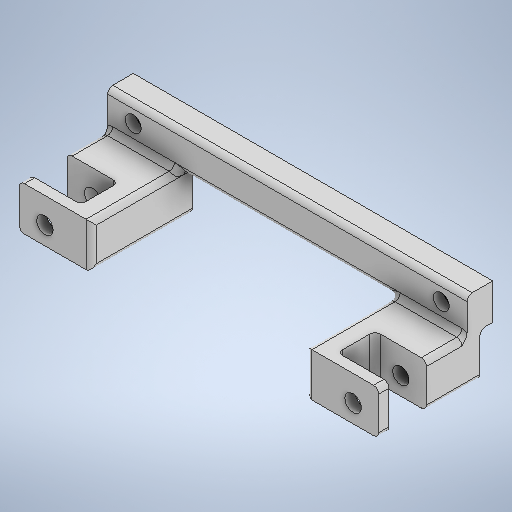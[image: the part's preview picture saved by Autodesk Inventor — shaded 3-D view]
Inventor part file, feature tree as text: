
AUTODESK INVENTOR PART (.ipt)
format: ipt  version: 2025.1 (Build 291241000, 241)  size: 368,128 bytes
history: native  units: mm
features: extrude x5, sketch x3, plane x1, fillet x1, mirror x1, projected_geometry x1
ambient origin geometry x8: Origin, YZ Plane, XZ Plane, XY Plane, X Axis, Y Axis, Z Axis, Center Point
bodies: Solid1 (feature_tree)
feature tree (12):
  sketch  "Sketch1"  dims[d0=4.85mm d1=30.0mm]
  extrude  "Extrusion1"  Depth=30.0mm
  extrude  "Extrusion2"  Depth=3.2mm
  extrude  "Extrusion3"  Depth=1.0mm
  extrude  "Extrusion4"  Depth=1.0mm
  plane  "Work Plane1"
  extrude  "Extrusion5"  TaperAngle=0.0deg  [1 undecoded]
  fillet  "Fillet1"  Radius=3.5mm
  mirror  "Mirror1"
  sketch  "Sketch2"  dims[d2=3.1mm d3=3.2mm]
  sketch  "Sketch4"  dims[d4=0.0mm d5=8.5mm d6=35.0mm d7=0.0mm d8=3.5mm d9=3.5mm d10=0.0mm d11=14.0mm d12=3.5mm d13=4.0mm d14=5.0mm d15=0.0mm d16=3.0mm d17=0.0mm d18=2.5mm d19=0.0mm d20=17.2mm d21=0.0mm d22=-2.0mm d23=5.0mm d24=7.3mm d25=0.0mm d26=1.0mm]
  projected_geometry  "Projected Loop1"
note: 1 required parameter value undecoded (feature->parameter linkage not recoverable at this tier; creation-order binding heuristic only, values carry confidence <= 0.55)
